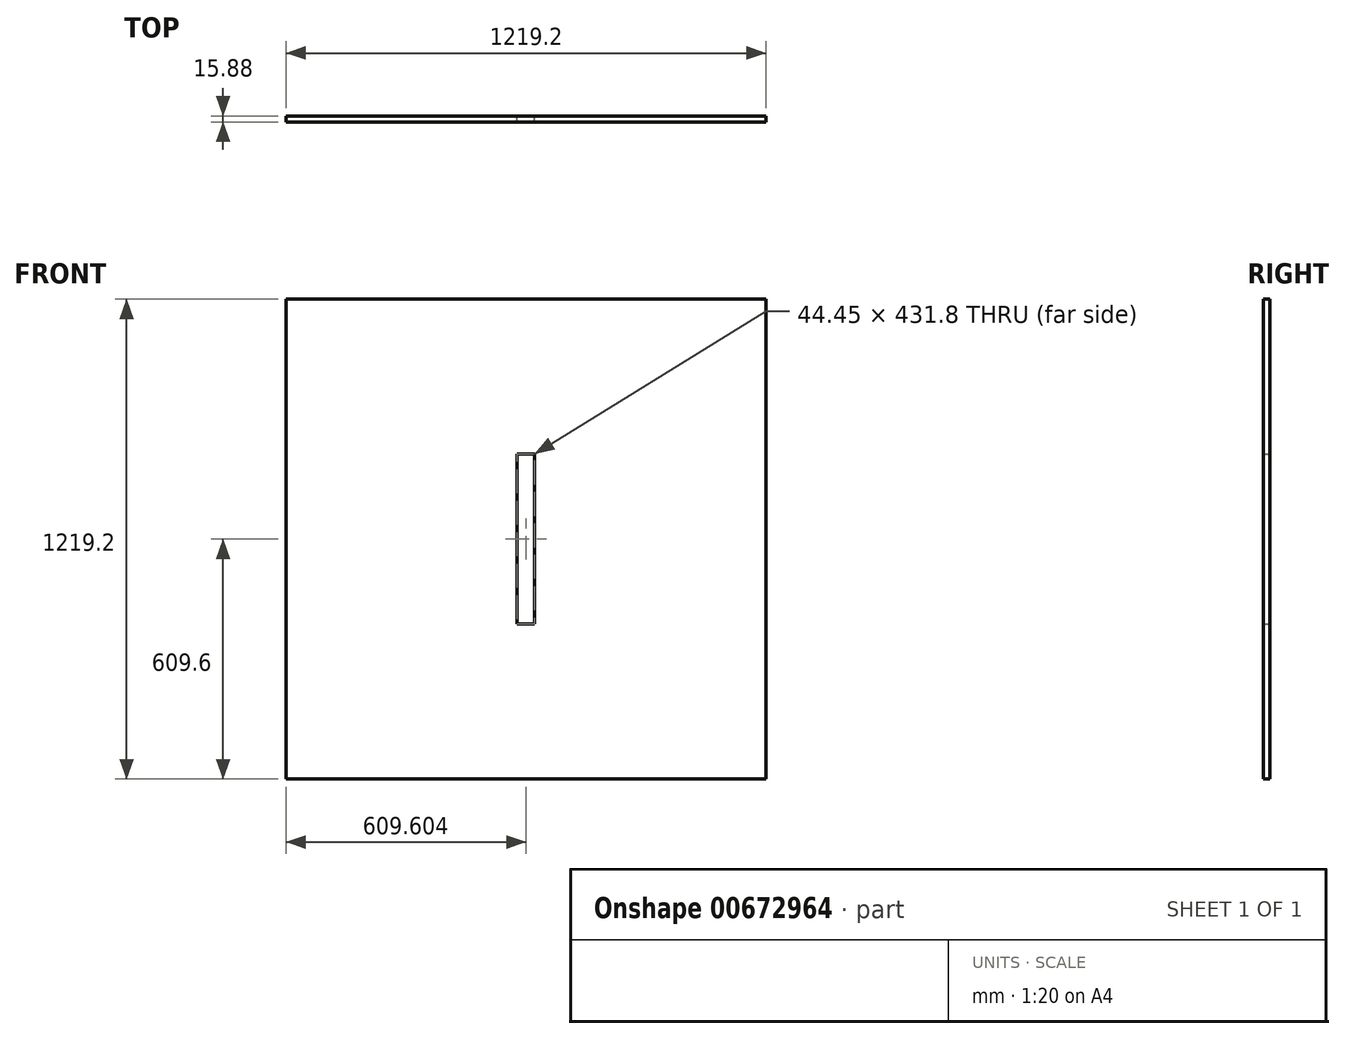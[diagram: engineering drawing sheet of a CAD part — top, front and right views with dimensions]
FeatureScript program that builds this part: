
annotation { "Feature Type Name" : "Feature", "Feature Type Description" : "" }
export const myFeature = defineFeature(function(context is Context, id is Id, definition is map)
    precondition{}
    {
        {
            var Q0;
            Q0=qCreatedBy(makeId("Front.planeOp"),FACE);
            var sketch = newSketch(context, id + "F0", { "sketchPlane" : qUnion([Q0])});
            skLineSegment(sketch, "E0.bottom", {"start": v(-13.42, 0) * mm, "end": v(-1232.62, 0) * mm});
            skLineSegment(sketch, "E0.top", {"start": v(-13.42, 1219.2) * mm, "end": v(-1232.62, 1219.2) * mm});
            skLineSegment(sketch, "E0.left", {"start": v(-13.42, 0) * mm, "end": v(-13.42, 1219.2) * mm});
            skLineSegment(sketch, "E0.right", {"start": v(-1232.62, 0) * mm, "end": v(-1232.62, 1219.2) * mm});
            skLineSegment(sketch, "E1.bottom", {"start": v(-645.24, 825.5) * mm, "end": v(-600.8, 825.5) * mm});
            skLineSegment(sketch, "E1.top", {"start": v(-645.24, 393.7) * mm, "end": v(-600.8, 393.7) * mm});
            skLineSegment(sketch, "E1.left", {"start": v(-645.24, 825.5) * mm, "end": v(-645.24, 393.7) * mm});
            skLineSegment(sketch, "E1.right", {"start": v(-600.8, 825.5) * mm, "end": v(-600.8, 393.7) * mm});
            skSolve(sketch);
        }
        {
            var Q0;
            Q0=makeQuery(id+"F0.imprint","IMPRINT",FACE,{"disambiguationData":[TD([[makeQuery(id+"F0.imprint","IMPRINT",EDGE,{"derivedFrom":sQuery(id+"F0.wireOp",EDGE,"E0.bottom")}),-1.0]])]});
            extrude(context, id + "F1", {"entities" : qUnion([Q0]), "depth" : 15.88 * mm, "offsetDistance" : 25.4 * mm});
        }
    });
